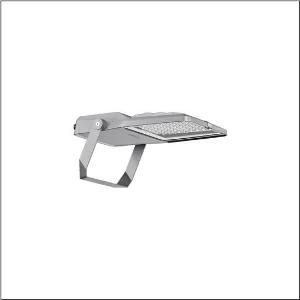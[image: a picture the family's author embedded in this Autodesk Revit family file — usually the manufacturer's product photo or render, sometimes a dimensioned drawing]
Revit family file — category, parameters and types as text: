
# Revit family: floodlight_fl_21_mini___pl61_5xa7773c2c1a_b950
name_source: partatom
category: Lighting Fixtures
units: mm (PartAtom-declared; Revit-internal decimal feet)

## family parameters
Cut with Voids When Loaded = No
Host = Face
Light Source = No
Part Type = Normal
Room Calculation Point = No
Round Connector Dimension = Use Diameter
Shared = No

## types (1)
- --- (1 x LED, 19150 lm, 163.5 W, 3000K)
    Apparent Load = 163 VA
    CIE Flux Codes = 33 65 98 100 100
    Color Rendering = 70
    Color Temperature = 3000K
    Default Elevation = 1800 mm
    Description = Floodlight FL 21 mini, floodlight, primary light control with lens, of PMMA, primary optical cover: protective disc, of toughened safety glass, transparent, light distribution: PL61, light emission: direct distribution, installation type: surface-mounted, LED, High Power LED, rated luminous flux: 19.150lm, luminous efficacy: 117lm/W, light colour: 730, colour temperature: 3000K, control: Temp-Guard, with terminal, 6-pole, mains connection: 220..240V, AC, 50/60Hz, start of lifetime: 164W, luminaire housing, of diecast aluminium, powder-coated, Siteco® metallic grey (DB 702S), corrosivity category C5 mid according to DIN EN ISO 12944, sealing non-destructively replaceable, mounting bracket, of steel, galvanised, powder-coated, Siteco® metallic grey (DB 702S), ON/OFF, protection rating (complete): IP66, insulation class (complete): insulation class I (protective earthing), certification: CE, ENEC, VDE, protection symbol: D, impact resistance: IK08, permissible operating ambient temperature: -40..+40°C, permissible operating ambient temperature for outdoor applications: -40..+50°C, standard: DIN EN 12944, LABS conformity tested according to VDMA 24364:2018-05, packaging unit: 1 piece

Light Distribution: PL61
    Height = 70 mm
    Lamp = 1 x LED
    Lamp Light Flux = 19150 lm
    Lamp Power = 163.5 W
    Lamp count = 1
    Length = 485 mm
    Luminous efficacy = 117 lm/W
    Manufacturer = Siteco
    ModVariant = No
    Model = 5XA7773C2C1A
    Number of Poles = 1
    OnlyDefault = Yes
    Power Factor = 1
    Product Name = Floodlight FL 21 mini | PL61
    Product group = floodlight | pylon annexe
    ProductGroupID = 6200
    Protection Class = Protection class I
    Protection Degree = IP 66
    RLX_Detail_Level = 1
    RLX_Emergency_Light_Flux = 0 lm
    RLX_Emergency_Type = 0
    RLX_Emergency_Type_DB = No
    RlxData = <blob elided: 94197 chars, md5=8b1401cd>
    Socket = socket
    Standby Power = 0 W
    System Light Flux = 19150 lm
    System Power = 163 W
    Type Comments = factory setting: luminous flux: 100 % | (ON | - | - | - | - | - | - | -) | 825 mA
    Type Image = l_1006845.jpg
    URL = http://relux.com
    VarID = @adj_123775
    Voltage = 0 V
    Weight = 0.00 kg
    Width = 337 mm

## geometry (parser evidence)
native form markers: Blend x4, Sweep x13
no freeform markers — native parametric forms only
